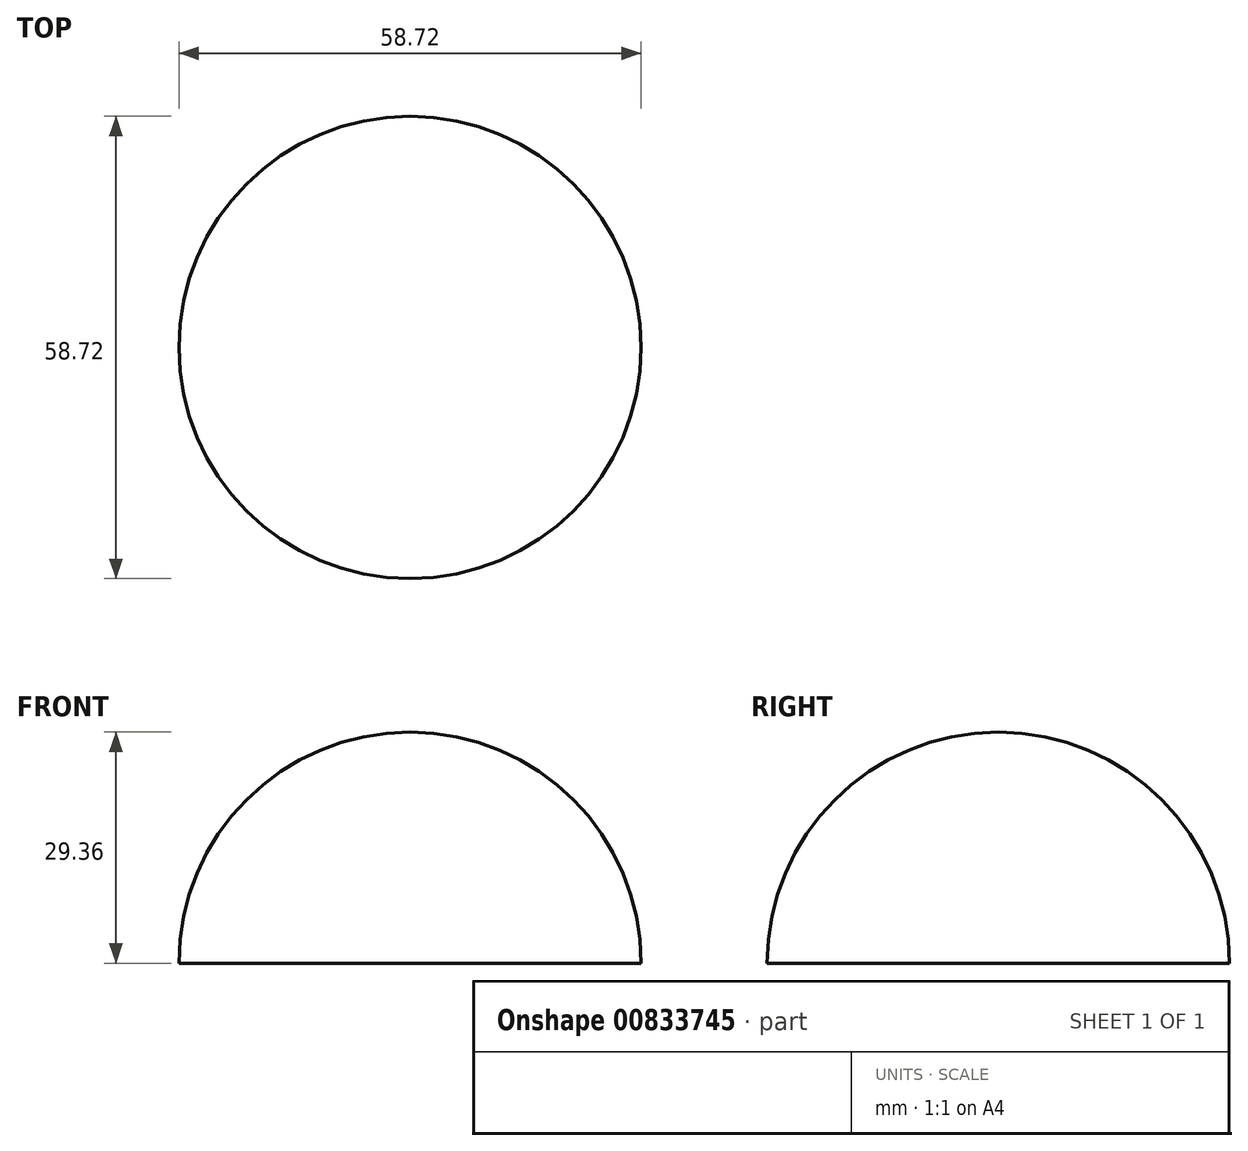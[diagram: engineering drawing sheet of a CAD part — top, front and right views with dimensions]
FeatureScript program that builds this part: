
annotation { "Feature Type Name" : "Feature", "Feature Type Description" : "" }
export const myFeature = defineFeature(function(context is Context, id is Id, definition is map)
    precondition{}
    {
        {
            var Q0;
            Q0=qCreatedBy(makeId("Top.planeOp"),FACE);
            var sketch = newSketch(context, id + "F0", { "sketchPlane" : qUnion([Q0])});
            skArc(sketch, "E0", {"start": v(-29.36, 0) * mm, "mid": v(0, 29.36) * mm, "end": v(29.36, 0) * mm});
            skLineSegment(sketch, "E1", {"start": v(-29.36, 0) * mm, "end": v(29.36, 0) * mm});
            skSolve(sketch);
        }
        {
            var Q0;
            Q0 = qSketchRegion(id + "F0", true);
            var Q1;
            Q1=makeQuery(id+"F0.imprint","IMPRINT",FACE,{"disambiguationData":[TD([[makeQuery(id+"F0.imprint","IMPRINT",EDGE,{"derivedFrom":sQuery(id+"F0.wireOp",EDGE,"E0")}),-1.0]])]});
            var Q2;
            Q2=sQuery(id+"F0.wireOp",EDGE,"E1");
            revolve(context, id + "F1", {"surfaceOperationType" : NewSurfaceOperationType.NEW, "entities" : qUnion([Q0, Q1]), "axis" : qUnion([Q2]), "revolveType" : RevolveType.ONE_DIRECTION, "angle" : 180 * degree});
        }
    });
